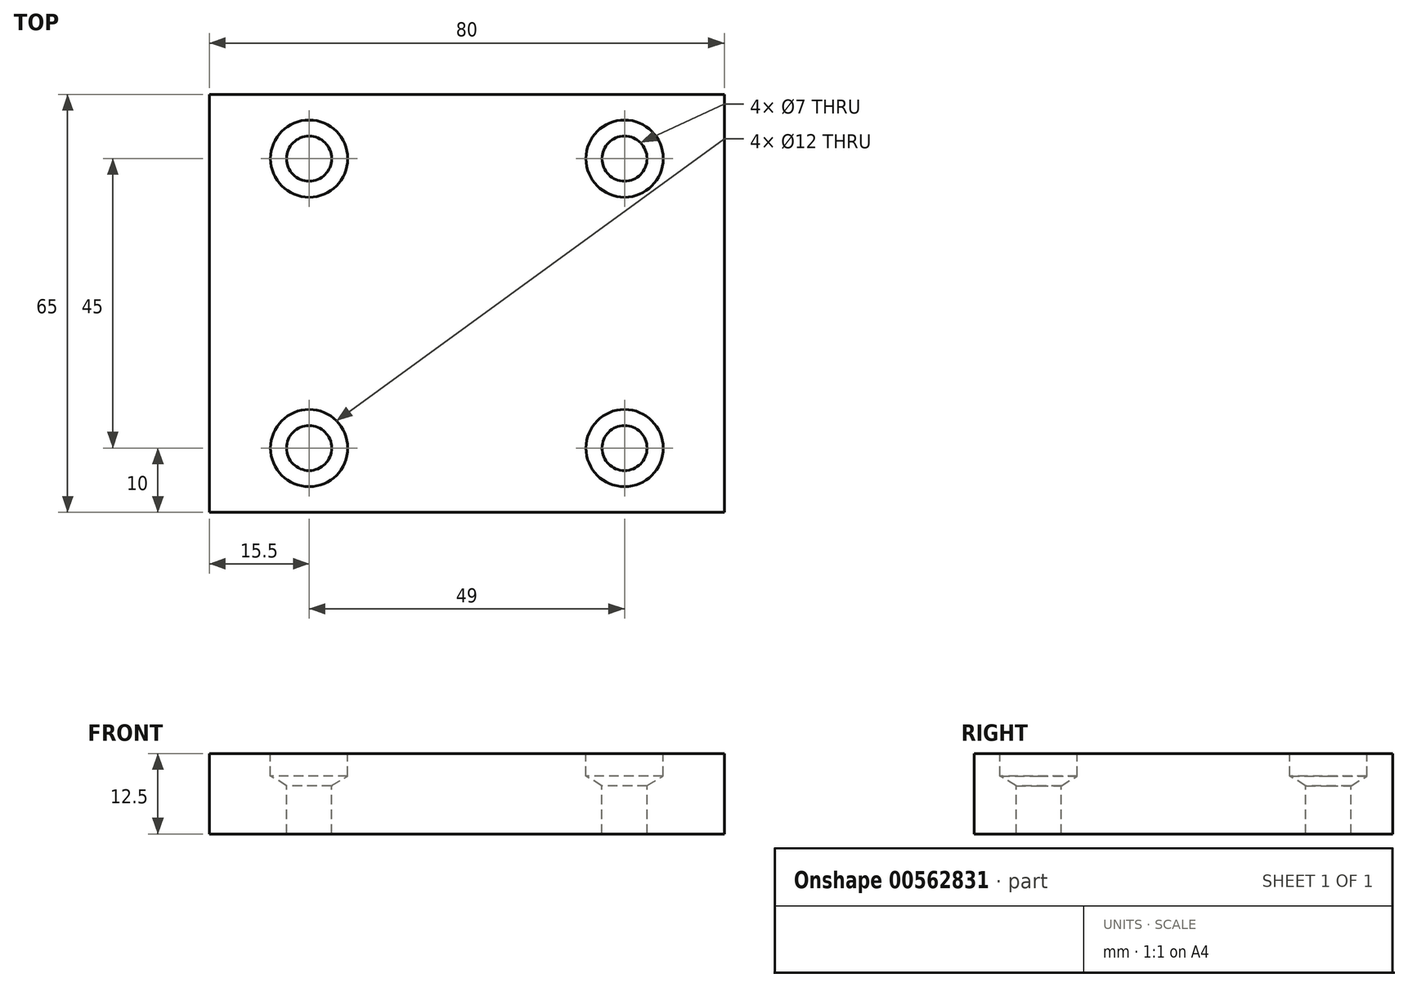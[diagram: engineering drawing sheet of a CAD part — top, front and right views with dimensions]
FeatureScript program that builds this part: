
annotation { "Feature Type Name" : "Feature", "Feature Type Description" : "" }
export const myFeature = defineFeature(function(context is Context, id is Id, definition is map)
    precondition{}
    {
        {
            var Q0;
            Q0=qCreatedBy(makeId("Top.planeOp"),FACE);
            var sketch = newSketch(context, id + "F0", { "sketchPlane" : qUnion([Q0])});
            skLineSegment(sketch, "E0.bottom", {"start": v(-40, 32.5) * mm, "end": v(40, 32.5) * mm});
            skLineSegment(sketch, "E0.top", {"start": v(-40, -32.5) * mm, "end": v(40, -32.5) * mm});
            skLineSegment(sketch, "E0.left", {"start": v(-40, 32.5) * mm, "end": v(-40, -32.5) * mm});
            skLineSegment(sketch, "E0.right", {"start": v(40, 32.5) * mm, "end": v(40, -32.5) * mm});
            skPoint(sketch, "E0.middle", {"position": v(0, 0) * mm});
            skCircle(sketch, "E1", {"center": v(-24.5, 22.5) * mm, "radius": 3.5 * mm});
            skCircle(sketch, "E2.MirrorC", {"center": v(24.5, 22.5) * mm, "radius": 3.5 * mm});
            skCircle(sketch, "E3.MirrorC", {"center": v(24.5, -22.5) * mm, "radius": 3.5 * mm});
            skCircle(sketch, "E4.MirrorC", {"center": v(-24.5, -22.5) * mm, "radius": 3.5 * mm});
            skSolve(sketch);
        }
        {
            var Q0;
            Q0 = qSketchRegion(id + "F0", true);
            extrude(context, id + "F1", {"entities" : qUnion([Q0]), "oppositeDirection" : true, "depth" : 12.5 * mm, "offsetDistance" : 25.4 * mm});
        }
        {
            var Q0;
            Q0=sQuery(id+"F0.wireOp",VERTEX,"E3.MirrorC.center");
            var Q1;
            Q1=sQuery(id+"F0.wireOp",VERTEX,"E4.MirrorC.center");
            var Q2;
            Q2=sQuery(id+"F0.wireOp",VERTEX,"E1.center");
            var Q3;
            Q3=sQuery(id+"F0.wireOp",VERTEX,"E2.MirrorC.center");
            var Q4;
            Q4=makeQuery(id+"F1.opExtrude","SWEPT_BODY",BODY,{"disambiguationData":[OSD([sQuery(id+"F0.wireOp",EDGE,"E0.bottom"),sQuery(id+"F0.wireOp",EDGE,"E0.top"),sQuery(id+"F0.wireOp",EDGE,"E0.left"),sQuery(id+"F0.wireOp",EDGE,"E0.right"),sQuery(id+"F0.wireOp",EDGE,"E1"),sQuery(id+"F0.wireOp",EDGE,"E2.MirrorC"),sQuery(id+"F0.wireOp",EDGE,"E3.MirrorC"),sQuery(id+"F0.wireOp",EDGE,"E4.MirrorC")])]});
            hole(context, id + "F2", {"style" : HoleStyle.SIMPLE, "endStyle" : HoleEndStyle.BLIND, "holeDiameter" : 12 * mm, "holeDepth" : 3.5 * mm, "isTappedThrough" : true, "tappedDepth" : 12.7 * mm, "tapClearance" : 3, "locations" : qUnion([Q0, Q1, Q2, Q3]), "scope" : qUnion([Q4])});
        }
    });
